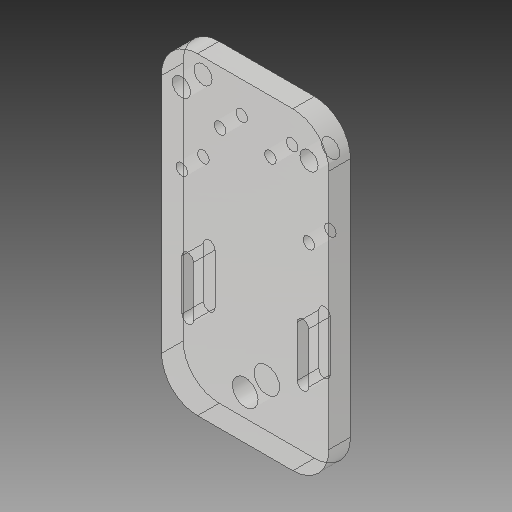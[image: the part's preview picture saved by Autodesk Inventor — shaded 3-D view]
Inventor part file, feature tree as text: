
AUTODESK INVENTOR PART (.ipt)
format: ipt  version: 2018 (Build 220112000, 112)  size: 196,096 bytes
history: native  units: mm
features: other x3, sketch x2
ambient origin geometry x8: Origin, YZ Plane, XZ Plane, XY Plane, X Axis, Y Axis, Z Axis, Center Point
bodies: Solid1 (feature_tree)
feature tree (5):
  other  "Hotend Front Plate revised_MIR.ipt"
  other  "Solid1::Hotend Front Plate revised_MIR.ipt"
  other  "TaggingFeature1"
  sketch  "Sketch1"  dims[d0=10.0mm]
  sketch  "Sketch2"
